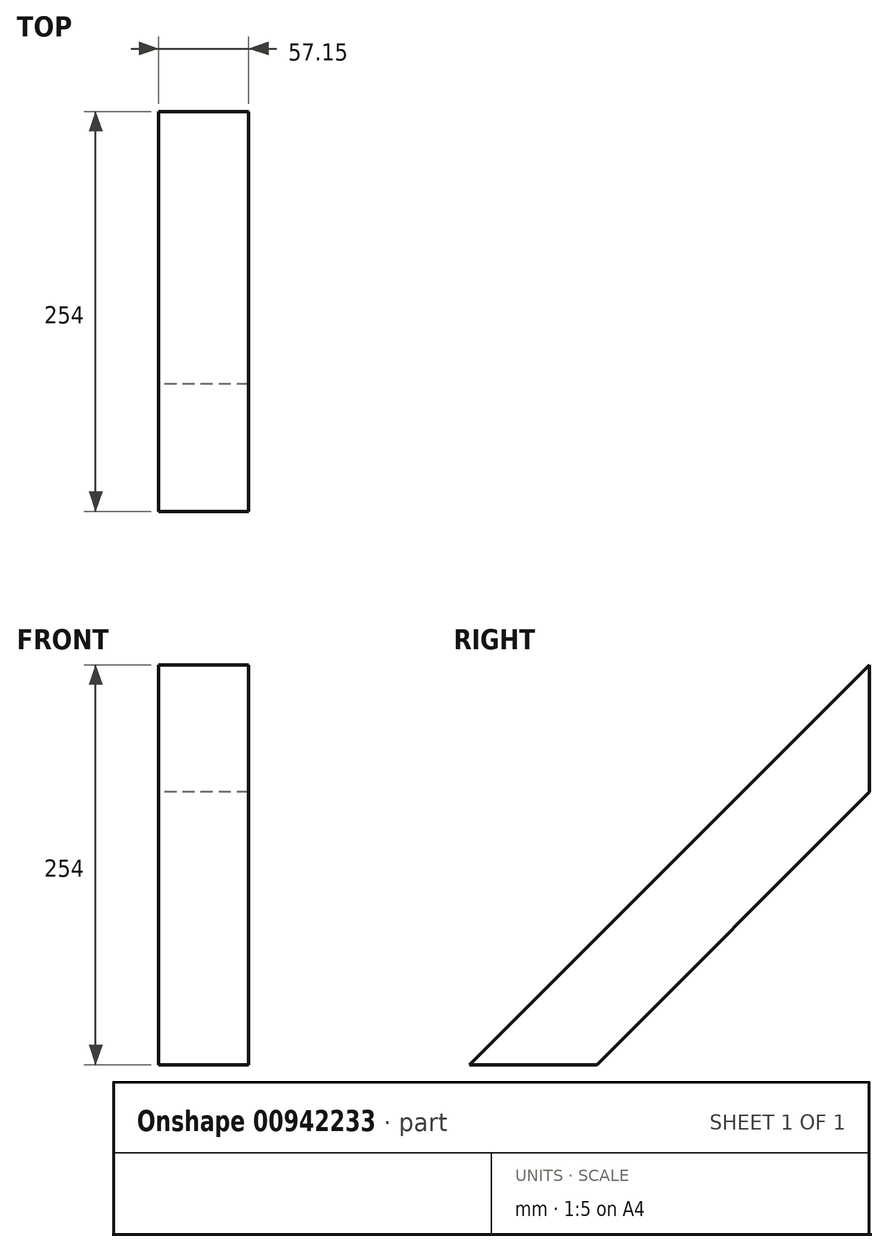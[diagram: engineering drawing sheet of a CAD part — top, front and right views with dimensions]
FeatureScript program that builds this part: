
annotation { "Feature Type Name" : "Feature", "Feature Type Description" : "" }
export const myFeature = defineFeature(function(context is Context, id is Id, definition is map)
    precondition{}
    {
        {
            var Q0;
            Q0=qCreatedBy(makeId("Right.planeOp"),FACE);
            var sketch = newSketch(context, id + "F0", { "sketchPlane" : qUnion([Q0])});
            skPoint(sketch, "E0.middle", {"position": v(0, 0) * mm});
            skLineSegment(sketch, "E1", {"start": v(-146.05, -146.05) * mm, "end": v(107.95, 107.95) * mm});
            skPoint(sketch, "E0.right.start.orphan", {"position": v(-146.05, 146.05) * mm});
            skLineSegment(sketch, "E2.0", {"start": v(-65.23, -146.05) * mm, "end": v(107.95, 27.13) * mm});
            skLineSegment(sketch, "E3", {"start": v(-146.05, -146.05) * mm, "end": v(-65.23, -146.05) * mm});
            skLineSegment(sketch, "E4", {"start": v(107.95, 27.13) * mm, "end": v(107.95, 107.95) * mm});
            skPoint(sketch, "E0.left.start.orphan", {"position": v(146.05, 146.05) * mm});
            skLineSegment(sketch, "E5.trimOffspring", {"start": v(-65.23, -146.05) * mm, "end": v(-146.05, -146.05) * mm});
            skPoint(sketch, "E0.top.start.orphan", {"position": v(146.05, -146.05) * mm});
            skPoint(sketch, "E6.orphan", {"position": v(107.95, -146.05) * mm});
            skSolve(sketch);
        }
        {
            var Q0;
            Q0 = qSketchRegion(id + "F0", true);
            extrude(context, id + "F1", {"entities" : qUnion([Q0]), "depth" : 57.15 * mm, "offsetDistance" : 25.4 * mm});
        }
    });
